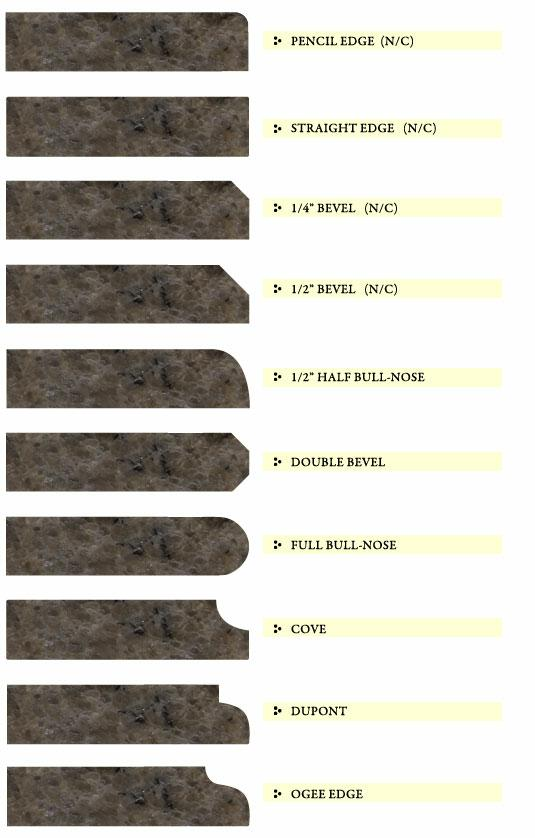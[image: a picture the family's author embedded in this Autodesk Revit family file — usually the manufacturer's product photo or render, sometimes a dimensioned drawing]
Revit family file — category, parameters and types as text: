
# Revit family: Casework-DuPont-Corian-Straight-Countertop
name_source: partatom
category: Casework
revit_build: Autodesk Revit Architecture 2015 (Build: 20140903_1530(x64)
units: mm (PartAtom-declared; Revit-internal decimal feet)

## types (2) — shared parameters
1 2 Bevel = No
1 2 Half Bull Nose = No
1 4 Bevel = No
12B = No
12H = No
14B = No
C = No
Cove = No
D = No
DB = No
Description = Solid Surface Countertop
Double Bevel = No
Dupont = No
FBN = No
Full Bull Nose = No
Height = 3' - 0"
Manufacturer = DuPont
Model = Corian®
OE = No
Ogee Edge = No
PE = No
Pencil Edge = No
Product Name = Corian®
Product Page URL = http://www.dupont.com
SE = Yes
Straight Edge = Yes
zero-valued in all types: Cost

## per-type parameters (varying)
| type | Countertop Material | Depth | Thickness | URL |
| 1/2" | <By Category> | 2' - 0" | 0' - 0 1/2" | http://www.dupont.com |
| 3/4" | Solid Surface - DuPont - Corian - Glacier White 1/2" (12mm) | 2' - 6" | 0' - 1 3/16" | www.corian.com |

## geometry (parser evidence)
native form markers: Sweep x15
no freeform markers — native parametric forms only
